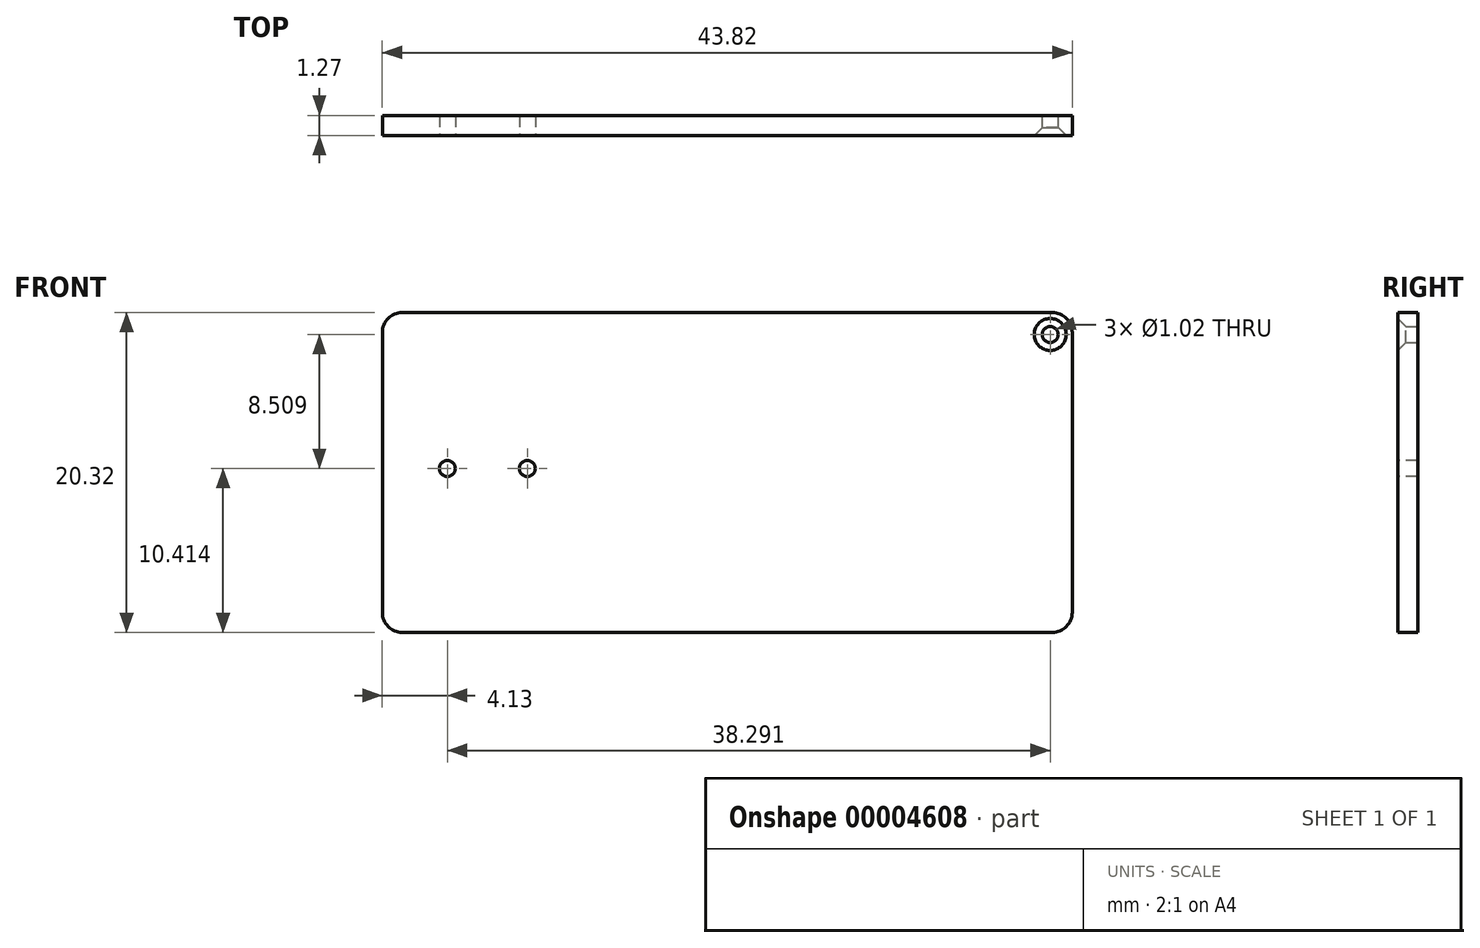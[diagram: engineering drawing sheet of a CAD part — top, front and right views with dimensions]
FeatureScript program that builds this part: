
annotation { "Feature Type Name" : "Feature", "Feature Type Description" : "" }
export const myFeature = defineFeature(function(context is Context, id is Id, definition is map)
    precondition{}
    {
        {
            var Q0;
            Q0=qCreatedBy(makeId("Front.planeOp"),FACE);
            var sketch = newSketch(context, id + "F0", { "sketchPlane" : qUnion([Q0])});
            skLineSegment(sketch, "E0.rect.bottom", {"start": v(21.9, -10.16) * mm, "end": v(-21.9, -10.16) * mm});
            skLineSegment(sketch, "E0.rect.top", {"start": v(21.9, 10.16) * mm, "end": v(-21.9, 10.16) * mm});
            skLineSegment(sketch, "E0.rect.left", {"start": v(21.9, -10.16) * mm, "end": v(21.9, 10.16) * mm});
            skLineSegment(sketch, "E0.rect.right", {"start": v(-21.9, -10.16) * mm, "end": v(-21.9, 10.16) * mm});
            skPoint(sketch, "E0.rect.middle", {"position": v(0, 0) * mm});
            skSolve(sketch);
        }
        {
            var Q0;
            Q0=makeQuery(id+"F0.imprint","IMPRINT",FACE,{"disambiguationData":[TD([[makeQuery(id+"F0.imprint","IMPRINT",EDGE,{"derivedFrom":sQuery(id+"F0.wireOp",EDGE,"E0.rect.bottom")}),-1.0]])]});
            extrude(context, id + "F1", {"entities" : qUnion([Q0]), "depth" : 1.27 * mm});
        }
        {
            var Q0;
            Q0=makeQuery(id+"F1.opExtrude","SWEPT_EDGE",EDGE,{"disambiguationData":[OSD([sQuery(id+"F0.wireOp",EDGE,"E0.rect.top"),sQuery(id+"F0.wireOp",EDGE,"E0.rect.left")])]});
            var Q1;
            Q1=makeQuery(id+"F1.opExtrude","SWEPT_EDGE",EDGE,{"disambiguationData":[OSD([sQuery(id+"F0.wireOp",EDGE,"E0.rect.bottom"),sQuery(id+"F0.wireOp",EDGE,"E0.rect.left")])]});
            var Q2;
            Q2=makeQuery(id+"F1.opExtrude","SWEPT_EDGE",EDGE,{"disambiguationData":[OSD([sQuery(id+"F0.wireOp",EDGE,"E0.rect.bottom"),sQuery(id+"F0.wireOp",EDGE,"E0.rect.right")])]});
            var Q3;
            Q3=makeQuery(id+"F1.opExtrude","SWEPT_EDGE",EDGE,{"disambiguationData":[OSD([sQuery(id+"F0.wireOp",EDGE,"E0.rect.top"),sQuery(id+"F0.wireOp",EDGE,"E0.rect.right")])]});
            fillet(context, id + "F2", {"entities" : qUnion([Q0, Q1, Q2, Q3]), "radius" : 1.27 * mm, "tangentPropagation" : true, "allowEdgeOverflow" : false});
        }
        {
            var Q0;
            Q0=qCreatedBy(makeId("Front.planeOp"),FACE);
            var sketch = newSketch(context, id + "F3", { "sketchPlane" : qUnion([Q0])});
            skCircle(sketch, "E1", {"center": v(20.51, 8.76) * mm, "radius": 0.5 * mm});
            skCircle(sketch, "E2.1.MirrorC", {"center": v(20.51, -8.76) * mm, "radius": 0.5 * mm});
            skSolve(sketch);
        }
        {
            var Q0;
            {Q0=qUnion([makeQuery(id+"F3.imprint","IMPRINT",FACE,{"disambiguationData":[TD([[makeQuery(id+"F3.imprint","IMPRINT",EDGE,{"derivedFrom":sQuery(id+"F3.wireOp",EDGE,"E1")}),1.0]])]}),makeQuery(id+"F3.imprint","IMPRINT",FACE,{"disambiguationData":[TD([[makeQuery(id+"F3.imprint","IMPRINT",EDGE,{"derivedFrom":sQuery(id+"F3.wireOp",EDGE,"E2.1.MirrorC")}),-1.0]])]})]);}
            extrude(context, id + "F4", {"entities" : qUnion([Q0]), "operationType" : NewBodyOperationType.REMOVE, "endBound" : BoundingType.THROUGH_ALL, "depth" : 25.4 * mm});
        }
        {
            var Q0;
            Q0=makeQuery(id+"F1.opExtrude","CAP_FACE",FACE,{"disambiguationData":[OSD([sQuery(id+"F0.wireOp",EDGE,"E0.rect.bottom"),sQuery(id+"F0.wireOp",EDGE,"E0.rect.top"),sQuery(id+"F0.wireOp",EDGE,"E0.rect.left"),sQuery(id+"F0.wireOp",EDGE,"E0.rect.right")])],"isStart":false});
            var sketch = newSketch(context, id + "F5", { "sketchPlane" : qUnion([Q0])});
            skCircle(sketch, "E3", {"center": v(-17.78, 0.25) * mm, "radius": 0.5 * mm});
            skCircle(sketch, "E4", {"center": v(-12.7, 0.25) * mm, "radius": 0.5 * mm});
            skLineSegment(sketch, "E5", {"start": v(-17.78, 0.25) * mm, "end": v(-12.7, 0.25) * mm, "construction": true});
            skSolve(sketch);
        }
        {
            var Q0;
            {Q0=qUnion([makeQuery(id+"F5.imprint","IMPRINT",FACE,{"disambiguationData":[TD([[makeQuery(id+"F5.imprint","IMPRINT",EDGE,{"derivedFrom":sQuery(id+"F5.wireOp",EDGE,"E3")}),1.0]])]}),makeQuery(id+"F5.imprint","IMPRINT",FACE,{"disambiguationData":[TD([[makeQuery(id+"F5.imprint","IMPRINT",EDGE,{"derivedFrom":sQuery(id+"F5.wireOp",EDGE,"E4")}),1.0]])]})]);}
            extrude(context, id + "F6", {"entities" : qUnion([Q0]), "operationType" : NewBodyOperationType.REMOVE, "endBound" : BoundingType.THROUGH_ALL, "oppositeDirection" : true, "depth" : 25.4 * mm});
        }
        {
            var Q0;
            Q0=makeQuery(id+"F4.boolean.opBoolean","INTERSECT",EDGE,{"derivedFrom":[makeQuery(id+"F1.opExtrude","CAP_FACE",FACE,{"disambiguationData":[OSD([sQuery(id+"F0.wireOp",EDGE,"E0.rect.bottom"),sQuery(id+"F0.wireOp",EDGE,"E0.rect.top"),sQuery(id+"F0.wireOp",EDGE,"E0.rect.left"),sQuery(id+"F0.wireOp",EDGE,"E0.rect.right")])],"isStart":false}),makeQuery(id+"F4.opExtrude","SWEPT_FACE",FACE,{"disambiguationData":[OSD([sQuery(id+"F3.wireOp",EDGE,"E1")])]})]});
            var Q1;
            Q1=makeQuery(id+"F4.boolean.opBoolean","INTERSECT",EDGE,{"derivedFrom":[makeQuery(id+"F1.opExtrude","CAP_FACE",FACE,{"disambiguationData":[OSD([sQuery(id+"F0.wireOp",EDGE,"E0.rect.bottom"),sQuery(id+"F0.wireOp",EDGE,"E0.rect.top"),sQuery(id+"F0.wireOp",EDGE,"E0.rect.left"),sQuery(id+"F0.wireOp",EDGE,"E0.rect.right")])],"isStart":false}),makeQuery(id+"F4.opExtrude","SWEPT_FACE",FACE,{"disambiguationData":[OSD([sQuery(id+"F3.wireOp",EDGE,"E2.1.MirrorC")])]})]});
            var Q2;
            Q2=makeQuery(id+"F6.boolean.opBoolean","COPY",EDGE,{"derivedFrom":makeQuery(id+"F6.opExtrude","CAP_EDGE",EDGE,{"disambiguationData":[OSD([sQuery(id+"F5.wireOp",EDGE,"E3")])],"isStart":true})});
            var Q3;
            Q3=makeQuery(id+"F6.boolean.opBoolean","COPY",EDGE,{"derivedFrom":makeQuery(id+"F6.opExtrude","CAP_EDGE",EDGE,{"disambiguationData":[OSD([sQuery(id+"F5.wireOp",EDGE,"E4")])],"isStart":true})});
            chamfer(context, id + "F7", {"entities" : qUnion([Q0, Q1, Q2, Q3]), "width" : 0.5 * mm, "tangentPropagation" : true});
        }
    });
